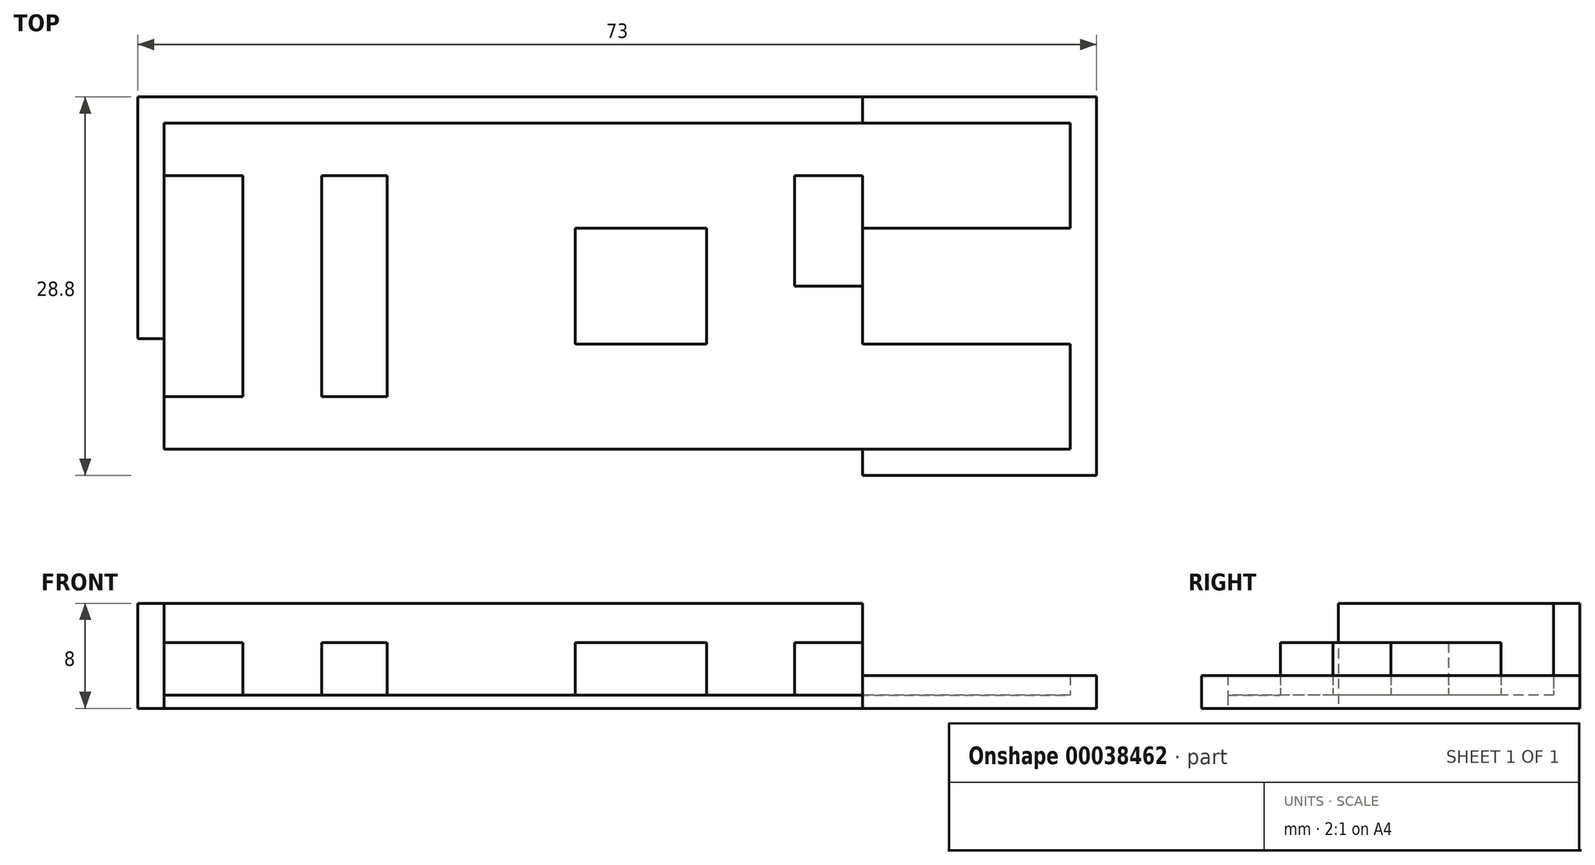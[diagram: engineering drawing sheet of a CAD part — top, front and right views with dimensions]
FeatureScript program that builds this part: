
annotation { "Feature Type Name" : "Feature", "Feature Type Description" : "" }
export const myFeature = defineFeature(function(context is Context, id is Id, definition is map)
    precondition{}
    {
        {
            var Q0;
            Q0=qCreatedBy(makeId("Top.planeOp"),FACE);
            var sketch = newSketch(context, id + "F0", { "sketchPlane" : qUnion([Q0])});
            skLineSegment(sketch, "E0", {"start": v(0, 4) * mm, "end": v(64, 4) * mm, "construction": true});
            skLineSegment(sketch, "E1", {"start": v(0, 20.8) * mm, "end": v(53.2, 20.8) * mm, "construction": true});
            skLineSegment(sketch, "E2", {"start": v(41.3, 20.8) * mm, "end": v(41.3, 4) * mm, "construction": true});
            skLineSegment(sketch, "E3.bottom", {"start": v(41.3, 16.8) * mm, "end": v(31.3, 16.8) * mm});
            skLineSegment(sketch, "E3.top", {"start": v(41.3, 8) * mm, "end": v(31.3, 8) * mm});
            skLineSegment(sketch, "E3.left", {"start": v(41.3, 16.8) * mm, "end": v(41.3, 8) * mm});
            skLineSegment(sketch, "E3.right", {"start": v(31.3, 16.8) * mm, "end": v(31.3, 8) * mm});
            skLineSegment(sketch, "E4.bottom", {"start": v(0, 20.8) * mm, "end": v(6, 20.8) * mm});
            skLineSegment(sketch, "E4.top", {"start": v(0, 4) * mm, "end": v(6, 4) * mm});
            skLineSegment(sketch, "E4.right", {"start": v(6, 20.8) * mm, "end": v(6, 4) * mm});
            skLineSegment(sketch, "E5.bottom", {"start": v(12, 20.8) * mm, "end": v(17, 20.8) * mm});
            skLineSegment(sketch, "E5.top", {"start": v(12, 4) * mm, "end": v(17, 4) * mm});
            skLineSegment(sketch, "E5.left", {"start": v(12, 20.8) * mm, "end": v(12, 4) * mm});
            skLineSegment(sketch, "E5.right", {"start": v(17, 20.8) * mm, "end": v(17, 4) * mm});
            skLineSegment(sketch, "E6.bottom", {"start": v(48, 20.8) * mm, "end": v(53.2, 20.8) * mm});
            skLineSegment(sketch, "E6.top", {"start": v(48, 12.4) * mm, "end": v(53.2, 12.4) * mm});
            skLineSegment(sketch, "E6.left", {"start": v(48, 20.8) * mm, "end": v(48, 12.4) * mm});
            skLineSegment(sketch, "E7", {"start": v(53.2, 50.95) * mm, "end": v(53.2, -26.15) * mm, "construction": true});
            skLineSegment(sketch, "E8", {"start": v(69, 59.43) * mm, "end": v(69, -48.28) * mm, "construction": true});
            skLineSegment(sketch, "E9", {"start": v(0, 53.08) * mm, "end": v(0, -48) * mm, "construction": true});
            skLineSegment(sketch, "E10", {"start": v(71, 54.69) * mm, "end": v(71, -59.79) * mm, "construction": true});
            skLineSegment(sketch, "E11", {"start": v(-24.24, -2) * mm, "end": v(101.32, -2) * mm, "construction": true});
            skLineSegment(sketch, "E12", {"start": v(-27.25, 26.8) * mm, "end": v(95.05, 26.8) * mm, "construction": true});
            skLineSegment(sketch, "E13", {"start": v(-2, 53.72) * mm, "end": v(-2, -68.22) * mm, "construction": true});
            skLineSegment(sketch, "E14", {"start": v(-39.18, 24.8) * mm, "end": v(95.54, 24.8) * mm, "construction": true});
            skLineSegment(sketch, "E15.left", {"start": v(0, 20.8) * mm, "end": v(0, 4) * mm});
            skLineSegment(sketch, "E16", {"start": v(53.2, 20.8) * mm, "end": v(53.2, 12.4) * mm});
            skLineSegment(sketch, "E17.bottom", {"start": v(69, 26.8) * mm, "end": v(71, 26.8) * mm});
            skLineSegment(sketch, "E17.top", {"start": v(69, -2) * mm, "end": v(71, -2) * mm});
            skLineSegment(sketch, "E17.left", {"start": v(69, 26.8) * mm, "end": v(69, -2) * mm});
            skLineSegment(sketch, "E17.right", {"start": v(71, 26.8) * mm, "end": v(71, -2) * mm});
            skLineSegment(sketch, "E18", {"start": v(83.68, 8) * mm, "end": v(51.38, 8) * mm, "construction": true});
            skLineSegment(sketch, "E19", {"start": v(82.66, 16.8) * mm, "end": v(49.28, 16.8) * mm, "construction": true});
            skLineSegment(sketch, "E20.bottom", {"start": v(53.2, 26.8) * mm, "end": v(69, 26.8) * mm});
            skLineSegment(sketch, "E20.top", {"start": v(53.2, 24.8) * mm, "end": v(69, 24.8) * mm});
            skLineSegment(sketch, "E20.left", {"start": v(53.2, 26.8) * mm, "end": v(53.2, 24.8) * mm});
            skLineSegment(sketch, "E20.right", {"start": v(69, 26.8) * mm, "end": v(69, 24.8) * mm});
            skLineSegment(sketch, "E21.top", {"start": v(53.2, 16.8) * mm, "end": v(69, 16.8) * mm});
            skLineSegment(sketch, "E21.left", {"start": v(53.2, 24.8) * mm, "end": v(53.2, 16.8) * mm});
            skLineSegment(sketch, "E21.right", {"start": v(69, 24.8) * mm, "end": v(69, 16.8) * mm});
            skLineSegment(sketch, "E22.top", {"start": v(53.2, 8) * mm, "end": v(69, 8) * mm});
            skLineSegment(sketch, "E22.left", {"start": v(53.2, 16.8) * mm, "end": v(53.2, 8) * mm});
            skLineSegment(sketch, "E22.right", {"start": v(69, 16.8) * mm, "end": v(69, 8) * mm});
            skLineSegment(sketch, "E23.top", {"start": v(53.2, 0) * mm, "end": v(69, 0) * mm});
            skLineSegment(sketch, "E23.left", {"start": v(53.2, 8) * mm, "end": v(53.2, 0) * mm});
            skLineSegment(sketch, "E23.right", {"start": v(69, 8) * mm, "end": v(69, 0) * mm});
            skLineSegment(sketch, "E24.top", {"start": v(53.2, -2) * mm, "end": v(69, -2) * mm});
            skLineSegment(sketch, "E24.left", {"start": v(53.2, 0) * mm, "end": v(53.2, -2) * mm});
            skLineSegment(sketch, "E24.right", {"start": v(69, 0) * mm, "end": v(69, -2) * mm});
            skLineSegment(sketch, "E25", {"start": v(53.2, 26.8) * mm, "end": v(-2, 26.8) * mm});
            skLineSegment(sketch, "E26", {"start": v(53.2, 24.8) * mm, "end": v(0, 24.8) * mm});
            skLineSegment(sketch, "E27", {"start": v(-8.82, 12.4) * mm, "end": v(3.3, 12.4) * mm, "construction": true});
            skLineSegment(sketch, "E28.bottom", {"start": v(-2, 16.4) * mm, "end": v(0, 16.4) * mm});
            skLineSegment(sketch, "E28.top", {"start": v(-2, 8.4) * mm, "end": v(0, 8.4) * mm});
            skLineSegment(sketch, "E28.left", {"start": v(-2, 16.4) * mm, "end": v(-2, 8.4) * mm});
            skLineSegment(sketch, "E28.right", {"start": v(0, 16.4) * mm, "end": v(0, 8.4) * mm});
            skLineSegment(sketch, "E29", {"start": v(0, 24.8) * mm, "end": v(0, 16.4) * mm});
            skLineSegment(sketch, "E30", {"start": v(-2, 16.4) * mm, "end": v(-2, 26.8) * mm});
            skLineSegment(sketch, "E31", {"start": v(-2, 8.4) * mm, "end": v(-2, -2) * mm});
            skLineSegment(sketch, "E32", {"start": v(-2, -2) * mm, "end": v(53.2, -2) * mm});
            skLineSegment(sketch, "E33", {"start": v(53.2, 0) * mm, "end": v(0, 0) * mm});
            skLineSegment(sketch, "E34", {"start": v(0, 0) * mm, "end": v(0, 4) * mm});
            skSolve(sketch);
        }
        {
            var Q0;
            {var subQ3=sQuery(id+"F0.wireOp",EDGE,"E20.top");Q0=makeQuery(id+"F0.imprint","IMPRINT",FACE,{"disambiguationData":[TD([[makeQuery(id+"F0.imprint","IMPRINT",EDGE,{"derivedFrom":subQ3}),-1.0]])]});}
            var Q1;
            Q1=makeQuery(id+"F0.imprint","IMPRINT",FACE,{"disambiguationData":[TD([[makeQuery(id+"F0.imprint","IMPRINT",EDGE,{"derivedFrom":sQuery(id+"F0.wireOp",EDGE,"E3.bottom")}),-1.0]])]});
            var Q2;
            Q2=makeQuery(id+"F0.imprint","IMPRINT",FACE,{"disambiguationData":[TD([[makeQuery(id+"F0.imprint","IMPRINT",EDGE,{"derivedFrom":sQuery(id+"F0.wireOp",EDGE,"E22.top")}),-1.0]])]});
            extrude(context, id + "F1", {"entities" : qUnion([Q0, Q1, Q2]), "depth" : 1 * mm});
        }
        {
            var Q0;
            Q0=makeQuery(id+"F0.imprint","IMPRINT",FACE,{"disambiguationData":[TD([[makeQuery(id+"F0.imprint","IMPRINT",EDGE,{"derivedFrom":sQuery(id+"F0.wireOp",EDGE,"E20.bottom")}),-1.0]])]});
            var Q1;
            {var subQ3=sQuery(id+"F0.wireOp",EDGE,"E21.top");Q1=makeQuery(id+"F0.imprint","IMPRINT",FACE,{"disambiguationData":[TD([[makeQuery(id+"F0.imprint","IMPRINT",EDGE,{"derivedFrom":subQ3}),-1.0]])]});}
            var Q2;
            Q2=makeQuery(id+"F0.imprint","IMPRINT",FACE,{"disambiguationData":[TD([[makeQuery(id+"F0.imprint","IMPRINT",EDGE,{"derivedFrom":sQuery(id+"F0.wireOp",EDGE,"E23.top")}),-1.0]])]});
            var Q3;
            Q3=makeQuery(id+"F0.imprint","IMPRINT",FACE,{"disambiguationData":[TD([[makeQuery(id+"F0.imprint","IMPRINT",EDGE,{"derivedFrom":sQuery(id+"F0.wireOp",EDGE,"E17.bottom")}),-1.0]])]});
            extrude(context, id + "F2", {"entities" : qUnion([Q0, Q1, Q2, Q3]), "operationType" : NewBodyOperationType.ADD, "depth" : 2.5 * mm});
        }
        {
            var Q0;
            {var subQ0=sQuery(id+"F0.wireOp",EDGE,"E4.bottom");Q0=makeQuery(id+"F0.imprint","IMPRINT",FACE,{"disambiguationData":[TD([[makeQuery(id+"F0.imprint","IMPRINT",EDGE,{"derivedFrom":subQ0}),-1.0]])]});}
            var Q1;
            Q1=makeQuery(id+"F0.imprint","IMPRINT",FACE,{"disambiguationData":[TD([[makeQuery(id+"F0.imprint","IMPRINT",EDGE,{"derivedFrom":sQuery(id+"F0.wireOp",EDGE,"E5.bottom")}),-1.0]])]});
            var Q2;
            Q2=makeQuery(id+"F0.imprint","IMPRINT",FACE,{"disambiguationData":[TD([[makeQuery(id+"F0.imprint","IMPRINT",EDGE,{"derivedFrom":sQuery(id+"F0.wireOp",EDGE,"E3.bottom")}),1.0]])]});
            var Q3;
            {var subQ1=sQuery(id+"F0.wireOp",EDGE,"E6.bottom");Q3=makeQuery(id+"F0.imprint","IMPRINT",FACE,{"disambiguationData":[TD([[makeQuery(id+"F0.imprint","IMPRINT",EDGE,{"derivedFrom":subQ1}),-1.0]])]});}
            extrude(context, id + "F3", {"entities" : qUnion([Q0, Q1, Q2, Q3]), "operationType" : NewBodyOperationType.ADD, "depth" : 5 * mm});
        }
        {
            var Q0;
            Q0=makeQuery(id+"F0.imprint","IMPRINT",FACE,{"disambiguationData":[TD([[makeQuery(id+"F0.imprint","IMPRINT",EDGE,{"derivedFrom":sQuery(id+"F0.wireOp",EDGE,"E25")}),1.0]])]});
            var Q1;
            Q1=makeQuery(id+"F0.imprint","IMPRINT",FACE,{"disambiguationData":[TD([[makeQuery(id+"F0.imprint","IMPRINT",EDGE,{"derivedFrom":sQuery(id+"F0.wireOp",EDGE,"E15.left")}),-1.0]])]});
            extrude(context, id + "F4", {"entities" : qUnion([Q0, Q1]), "operationType" : NewBodyOperationType.ADD, "depth" : 8 * mm});
        }
        {
            var Q0;
            Q0=makeQuery(id+"F0.imprint","IMPRINT",FACE,{"disambiguationData":[TD([[makeQuery(id+"F0.imprint","IMPRINT",EDGE,{"derivedFrom":sQuery(id+"F0.wireOp",EDGE,"E28.bottom")}),-1.0]])]});
            extrude(context, id + "F5", {"entities" : qUnion([Q0]), "operationType" : NewBodyOperationType.ADD, "depth" : 6 * mm});
        }
    });
